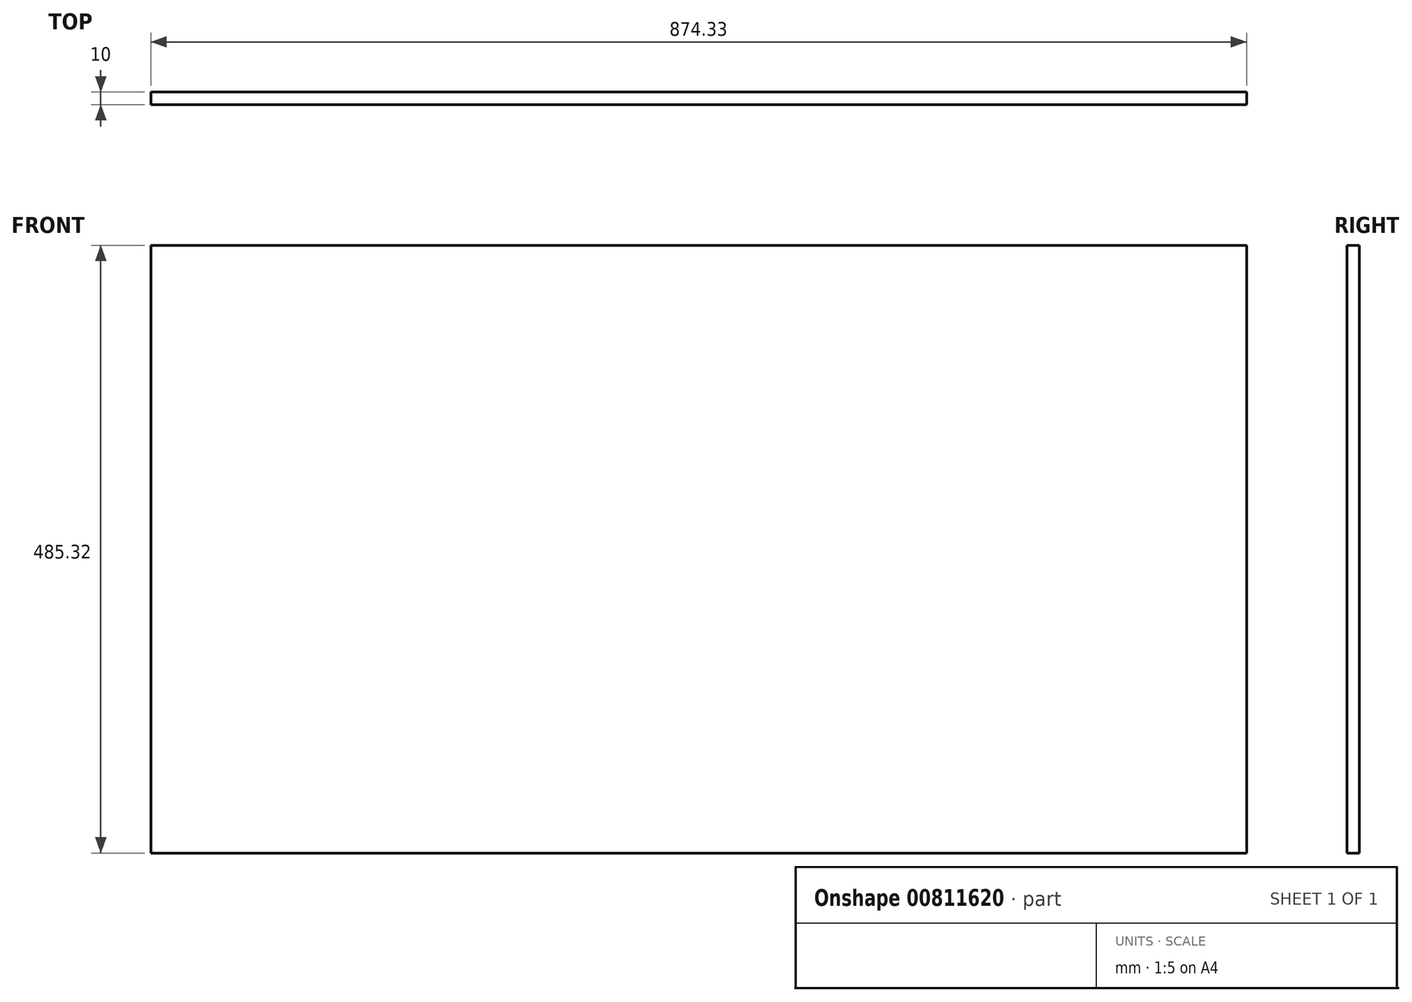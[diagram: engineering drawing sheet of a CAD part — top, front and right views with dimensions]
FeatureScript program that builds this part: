
annotation { "Feature Type Name" : "Feature", "Feature Type Description" : "" }
export const myFeature = defineFeature(function(context is Context, id is Id, definition is map)
    precondition{}
    {
        {
            var Q0;
            Q0=qCreatedBy(makeId("Front.planeOp"),FACE);
            var sketch = newSketch(context, id + "F0", { "sketchPlane" : qUnion([Q0])});
            skLineSegment(sketch, "E0.bottom", {"start": v(-389.41, 197.16) * mm, "end": v(484.92, 197.16) * mm});
            skLineSegment(sketch, "E0.top", {"start": v(-389.41, -288.16) * mm, "end": v(484.92, -288.16) * mm});
            skLineSegment(sketch, "E0.left", {"start": v(-389.41, 197.16) * mm, "end": v(-389.41, -288.16) * mm});
            skLineSegment(sketch, "E0.right", {"start": v(484.92, 197.16) * mm, "end": v(484.92, -288.16) * mm});
            skLineSegment(sketch, "E1", {"start": v(-389.41, 197.16) * mm, "end": v(484.92, -288.16) * mm});
            skSolve(sketch);
        }
        {
            var Q0;
            Q0=qSketchRegion(id+"F0",true);
            extrude(context, id + "F1", {"entities" : qUnion([Q0]), "depth" : 10 * mm});
        }
    });
